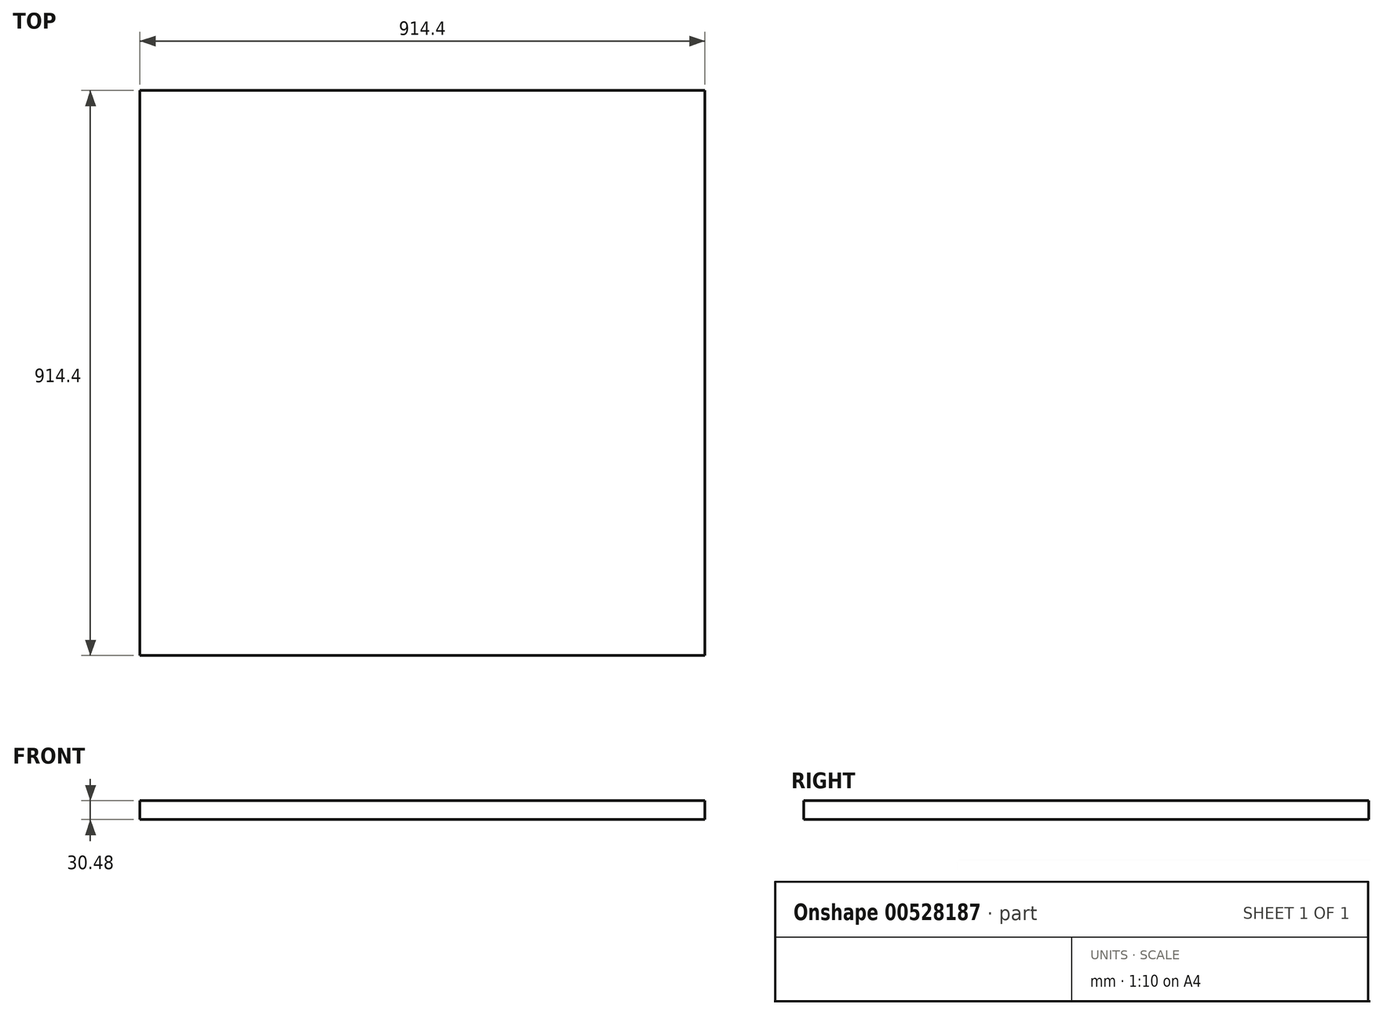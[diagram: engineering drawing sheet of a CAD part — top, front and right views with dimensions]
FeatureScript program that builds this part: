
annotation { "Feature Type Name" : "Feature", "Feature Type Description" : "" }
export const myFeature = defineFeature(function(context is Context, id is Id, definition is map)
    precondition{}
    {
        {
            var Q0;
            Q0=qCreatedBy(makeId("Top.planeOp"),FACE);
            var sketch = newSketch(context, id + "F0", { "sketchPlane" : qUnion([Q0])});
            skLineSegment(sketch, "E0.bottom", {"start": v(-465.13, 701.2) * mm, "end": v(449.27, 701.2) * mm});
            skLineSegment(sketch, "E0.top", {"start": v(-465.13, -213.2) * mm, "end": v(449.27, -213.2) * mm});
            skLineSegment(sketch, "E0.left", {"start": v(-465.13, 701.2) * mm, "end": v(-465.13, -213.2) * mm});
            skLineSegment(sketch, "E0.right", {"start": v(449.27, 701.2) * mm, "end": v(449.27, -213.2) * mm});
            skSolve(sketch);
        }
        {
            var Q0;
            Q0 = qSketchRegion(id + "F0", true);
            extrude(context, id + "F1", {"entities" : qUnion([Q0]), "depth" : 30.48 * mm, "offsetDistance" : 30.48 * mm});
        }
    });
